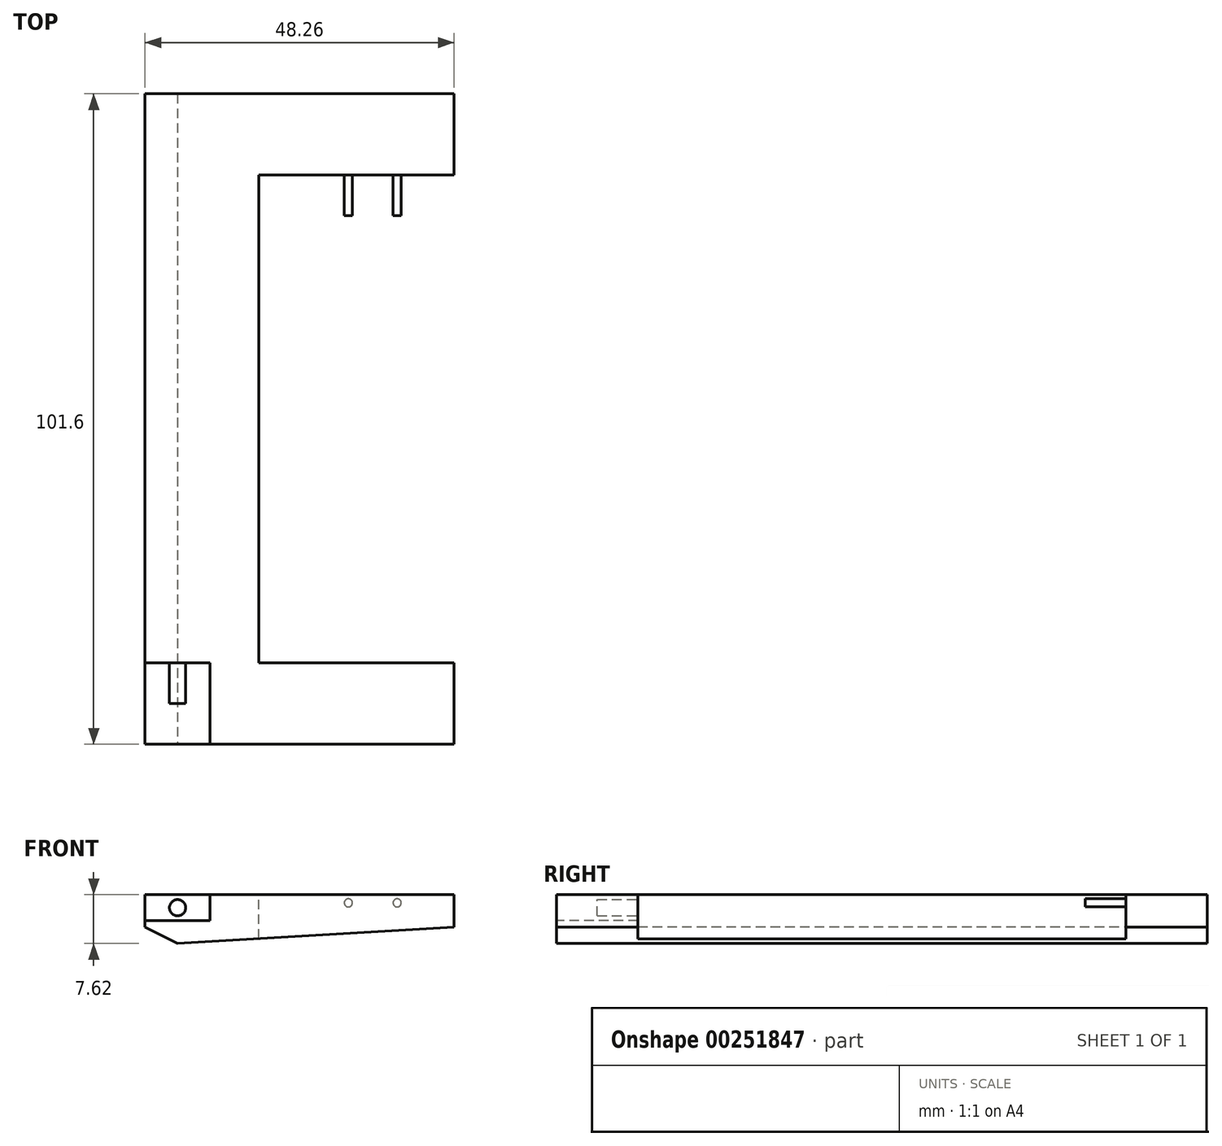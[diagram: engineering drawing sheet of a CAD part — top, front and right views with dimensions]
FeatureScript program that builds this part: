
annotation { "Feature Type Name" : "Feature", "Feature Type Description" : "" }
export const myFeature = defineFeature(function(context is Context, id is Id, definition is map)
    precondition{}
    {
        {
            var Q0;
            Q0=qCreatedBy(makeId("Front.planeOp"),FACE);
            var sketch = newSketch(context, id + "F0", { "sketchPlane" : qUnion([Q0])});
            skLineSegment(sketch, "E0", {"start": v(-2.54, 0.17) * mm, "end": v(-50.8, 0.17) * mm});
            skLineSegment(sketch, "E1", {"start": v(-50.8, 0.17) * mm, "end": v(-50.8, -4.9) * mm});
            skLineSegment(sketch, "E2", {"start": v(-50.8, -4.9) * mm, "end": v(-45.72, -7.45) * mm});
            skLineSegment(sketch, "E3", {"start": v(-45.72, -7.45) * mm, "end": v(-2.54, -4.9) * mm});
            skLineSegment(sketch, "E4", {"start": v(-2.54, -4.9) * mm, "end": v(-2.54, 0.17) * mm});
            skSolve(sketch);
        }
        {
            var Q0;
            Q0 = qSketchRegion(id + "F0", true);
            extrude(context, id + "F1", {"entities" : qUnion([Q0]), "endBound" : BoundingType.SYMMETRIC, "oppositeDirection" : true, "depth" : 101.6 * mm});
        }
        {
            var Q0;
            Q0=makeQuery(id+"F1.opExtrude","SWEPT_FACE",FACE,{"disambiguationData":[OSD([sQuery(id+"F0.wireOp",EDGE,"E0")])]});
            var sketch = newSketch(context, id + "F2", { "sketchPlane" : qUnion([Q0])});
            skLineSegment(sketch, "E5", {"start": v(-2.54, 38.1) * mm, "end": v(-33.02, 38.1) * mm});
            skLineSegment(sketch, "E6", {"start": v(-33.02, 38.1) * mm, "end": v(-33.02, 0) * mm});
            skLineSegment(sketch, "E7", {"start": v(-2.54, 38.1) * mm, "end": v(-2.54, 0) * mm});
            skLineSegment(sketch, "E8.MirrorCS", {"start": v(-2.54, -38.1) * mm, "end": v(-33.02, -38.1) * mm});
            skLineSegment(sketch, "E9.MirrorCS", {"start": v(-33.02, -38.1) * mm, "end": v(-33.02, 0) * mm});
            skLineSegment(sketch, "E10.MirrorCS", {"start": v(-2.54, -38.1) * mm, "end": v(-2.54, 0) * mm});
            skSolve(sketch);
        }
        {
            var Q0;
            Q0 = qSketchRegion(id + "F2", true);
            extrude(context, id + "F3", {"entities" : qUnion([Q0]), "operationType" : NewBodyOperationType.REMOVE, "endBound" : BoundingType.THROUGH_ALL, "oppositeDirection" : true, "depth" : 25.4 * mm});
        }
        {
            var Q0;
            Q0=makeQuery(id+"F1.opExtrude","CAP_FACE",FACE,{"disambiguationData":[OSD([sQuery(id+"F0.wireOp",EDGE,"E0"),sQuery(id+"F0.wireOp",EDGE,"E1"),sQuery(id+"F0.wireOp",EDGE,"E2"),sQuery(id+"F0.wireOp",EDGE,"E3"),sQuery(id+"F0.wireOp",EDGE,"E4")])],"isStart":true});
            var sketch = newSketch(context, id + "F4", { "sketchPlane" : qUnion([Q0])});
            skLineSegment(sketch, "E11.bottom", {"start": v(-50.8, 0.17) * mm, "end": v(-40.64, 0.17) * mm});
            skLineSegment(sketch, "E11.top", {"start": v(-50.8, -3.9) * mm, "end": v(-40.64, -3.9) * mm});
            skLineSegment(sketch, "E11.left", {"start": v(-50.8, 0.17) * mm, "end": v(-50.8, -3.9) * mm});
            skLineSegment(sketch, "E11.right", {"start": v(-40.64, 0.17) * mm, "end": v(-40.64, -3.9) * mm});
            skSolve(sketch);
        }
        {
            var Q0;
            Q0 = qSketchRegion(id + "F4", true);
            extrude(context, id + "F5", {"entities" : qUnion([Q0]), "operationType" : NewBodyOperationType.REMOVE, "oppositeDirection" : true, "depth" : 12.7 * mm});
        }
        {
            var Q0;
            Q0=makeQuery(id+"F5.boolean.opBoolean","COPY",FACE,{"derivedFrom":makeQuery(id+"F5.opExtrude","CAP_FACE",FACE,{"disambiguationData":[OSD([sQuery(id+"F4.wireOp",EDGE,"E11.bottom"),sQuery(id+"F4.wireOp",EDGE,"E11.top"),sQuery(id+"F4.wireOp",EDGE,"E11.left"),sQuery(id+"F4.wireOp",EDGE,"E11.right")])],"isStart":false})});
            var sketch = newSketch(context, id + "F6", { "sketchPlane" : qUnion([Q0])});
            skCircle(sketch, "E12", {"center": v(-45.72, -1.86) * mm, "radius": 1.27 * mm});
            skSolve(sketch);
        }
        {
            var Q0;
            Q0 = qSketchRegion(id + "F6", true);
            extrude(context, id + "F7", {"entities" : qUnion([Q0]), "operationType" : NewBodyOperationType.ADD, "depth" : 6.35 * mm});
        }
        {
            var Q0;
            Q0=makeQuery(id+"F3.boolean.opBoolean","COPY",FACE,{"derivedFrom":makeQuery(id+"F3.opExtrude","SWEPT_FACE",FACE,{"disambiguationData":[OSD([sQuery(id+"F2.wireOp",EDGE,"E5")])]})});
            var sketch = newSketch(context, id + "F8", { "sketchPlane" : qUnion([Q0])});
            skCircle(sketch, "E13", {"center": v(-19.05, -1.1) * mm, "radius": 0.64 * mm});
            skCircle(sketch, "E14", {"center": v(-11.43, -1.1) * mm, "radius": 0.64 * mm});
            skSolve(sketch);
        }
        {
            var Q0;
            Q0 = qSketchRegion(id + "F8", true);
            extrude(context, id + "F9", {"entities" : qUnion([Q0]), "operationType" : NewBodyOperationType.ADD, "depth" : 6.35 * mm});
        }
    });
